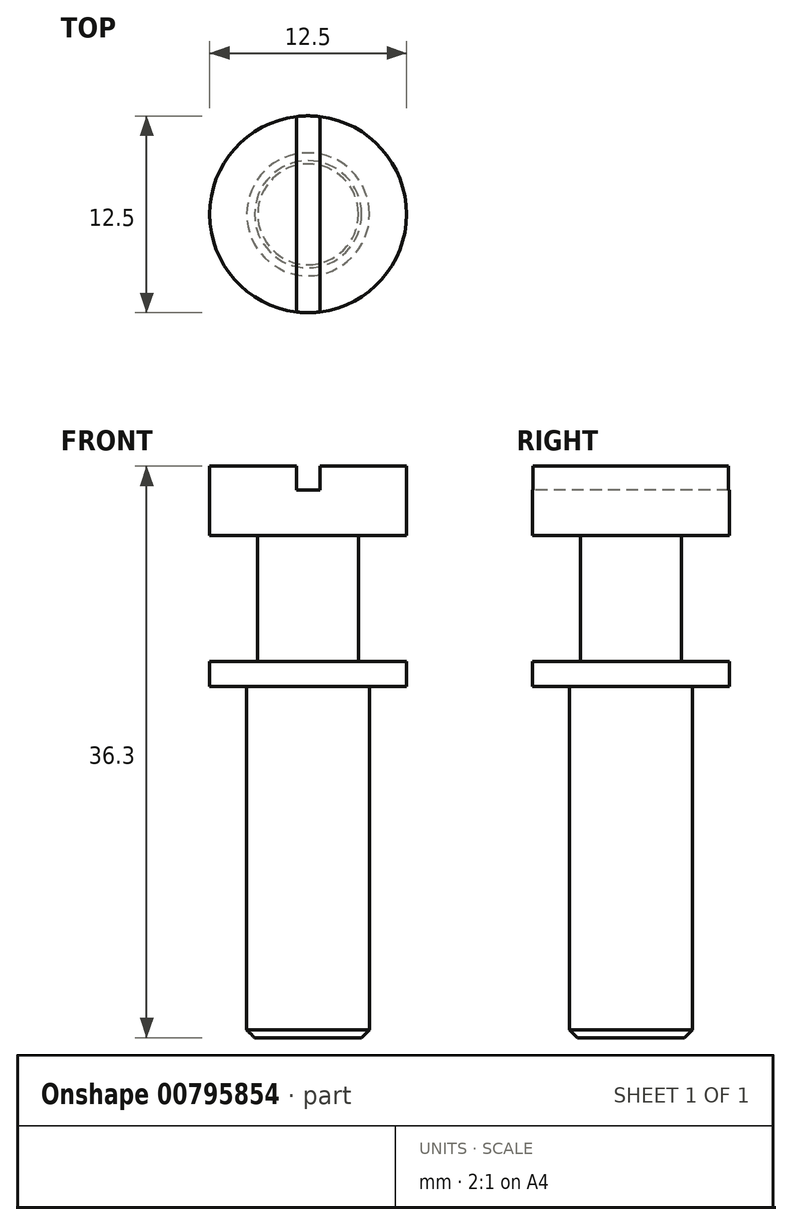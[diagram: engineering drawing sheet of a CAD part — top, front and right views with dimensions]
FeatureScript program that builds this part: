
annotation { "Feature Type Name" : "Feature", "Feature Type Description" : "" }
export const myFeature = defineFeature(function(context is Context, id is Id, definition is map)
    precondition{}
    {
        {
            var Q0;
            Q0=qCreatedBy(makeId("Front.planeOp"),FACE);
            var sketch = newSketch(context, id + "F0", { "sketchPlane" : qUnion([Q0])});
            skLineSegment(sketch, "E0", {"start": v(0, -18.15) * mm, "end": v(0, 18.15) * mm});
            skLineSegment(sketch, "E1", {"start": v(0, 18.15) * mm, "end": v(6.25, 18.15) * mm});
            skLineSegment(sketch, "E2", {"start": v(6.25, 18.15) * mm, "end": v(6.25, 13.75) * mm});
            skLineSegment(sketch, "E3", {"start": v(6.25, 13.75) * mm, "end": v(3.2, 13.75) * mm});
            skLineSegment(sketch, "E4", {"start": v(3.2, 13.75) * mm, "end": v(3.2, 5.75) * mm});
            skLineSegment(sketch, "E5", {"start": v(3.2, 5.75) * mm, "end": v(6.25, 5.75) * mm});
            skLineSegment(sketch, "E6", {"start": v(6.25, 5.75) * mm, "end": v(6.25, 4.15) * mm});
            skLineSegment(sketch, "E7", {"start": v(6.25, 4.15) * mm, "end": v(3.9, 4.15) * mm});
            skLineSegment(sketch, "E8", {"start": v(3.9, 4.15) * mm, "end": v(3.9, -17.65) * mm});
            skLineSegment(sketch, "E9", {"start": v(3.9, -17.65) * mm, "end": v(3.4, -18.15) * mm});
            skLineSegment(sketch, "E10", {"start": v(3.4, -18.15) * mm, "end": v(0, -18.15) * mm});
            skSolve(sketch);
        }
        {
            var Q0;
            Q0 = qSketchRegion(id + "F0", true);
            var Q1;
            Q1=sQuery(id+"F0.wireOp",EDGE,"E0");
            revolve(context, id + "F1", {"surfaceOperationType" : NewSurfaceOperationType.NEW, "entities" : qUnion([Q0]), "axis" : qUnion([Q1]), "revolveType" : RevolveType.FULL});
        }
        {
            var Q0;
            Q0=makeQuery(id+"F1.opRevolve","SWEPT_FACE",FACE,{"disambiguationData":[OSD([sQuery(id+"F0.wireOp",EDGE,"E1")])]});
            var sketch = newSketch(context, id + "F2", { "sketchPlane" : qUnion([Q0])});
            skLineSegment(sketch, "E11", {"start": v(0, 4.6) * mm, "end": v(0, -3.63) * mm, "construction": true});
            skLineSegment(sketch, "E12.bottom", {"start": v(-0.75, 6.5) * mm, "end": v(0.75, 6.5) * mm});
            skLineSegment(sketch, "E12.top", {"start": v(-0.75, -6.5) * mm, "end": v(0.75, -6.5) * mm});
            skLineSegment(sketch, "E12.left", {"start": v(-0.75, 6.5) * mm, "end": v(-0.75, -6.5) * mm});
            skLineSegment(sketch, "E12.right", {"start": v(0.75, 6.5) * mm, "end": v(0.75, -6.5) * mm});
            skSolve(sketch);
        }
        {
            var Q0;
            Q0 = qSketchRegion(id + "F2", true);
            extrude(context, id + "F3", {"entities" : qUnion([Q0]), "operationType" : NewBodyOperationType.REMOVE, "oppositeDirection" : true, "depth" : 1.5 * mm, "offsetDistance" : 25 * mm});
        }
    });
